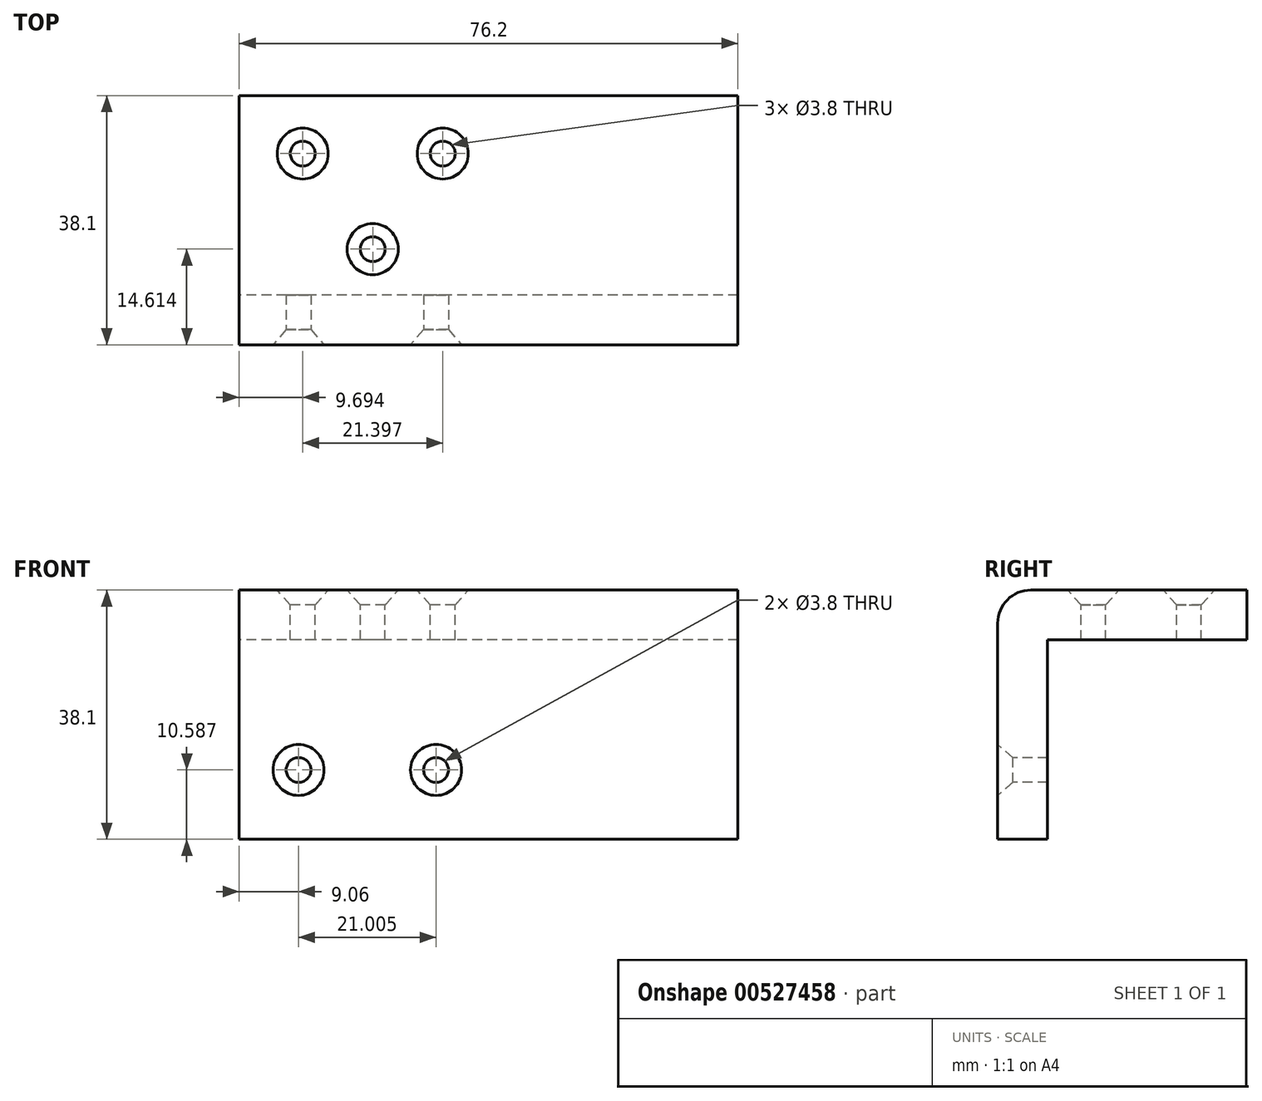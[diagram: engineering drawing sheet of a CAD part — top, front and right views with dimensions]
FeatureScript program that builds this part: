
annotation { "Feature Type Name" : "Feature", "Feature Type Description" : "" }
export const myFeature = defineFeature(function(context is Context, id is Id, definition is map)
    precondition{}
    {
        {
            var Q0;
            Q0=qCreatedBy(makeId("Right.planeOp"),FACE);
            var sketch = newSketch(context, id + "F0", { "sketchPlane" : qUnion([Q0])});
            skLineSegment(sketch, "E0.bottom", {"start": v(-7.62, 7.62) * mm, "end": v(30.48, 7.62) * mm});
            skLineSegment(sketch, "E0.top", {"start": v(-7.62, -30.48) * mm, "end": v(0, -30.48) * mm});
            skLineSegment(sketch, "E0.left", {"start": v(-7.62, 7.62) * mm, "end": v(-7.62, -30.48) * mm});
            skLineSegment(sketch, "E0.right", {"start": v(30.48, 7.62) * mm, "end": v(30.48, 0) * mm});
            skLineSegment(sketch, "E1", {"start": v(0, -30.48) * mm, "end": v(0, 0) * mm});
            skLineSegment(sketch, "E2", {"start": v(0, 0) * mm, "end": v(30.48, 0) * mm});
            skSolve(sketch);
        }
        {
            var Q0;
            Q0=makeQuery(id+"F0.imprint","IMPRINT",FACE,{"disambiguationData":[TD([[makeQuery(id+"F0.imprint","IMPRINT",EDGE,{"derivedFrom":sQuery(id+"F0.wireOp",EDGE,"E0.bottom")}),-1.0]])]});
            extrude(context, id + "F1", {"entities" : qUnion([Q0]), "endBound" : BoundingType.SYMMETRIC, "depth" : 76.2 * mm, "offsetDistance" : 25.4 * mm});
        }
        {
            var Q0;
            Q0=makeQuery(id+"F1.opExtrude","SWEPT_FACE",FACE,{"disambiguationData":[OSD([sQuery(id+"F0.wireOp",EDGE,"E0.bottom")])]});
            var sketch = newSketch(context, id + "F2", { "sketchPlane" : qUnion([Q0])});
            skLineSegment(sketch, "E3.bottom", {"start": v(-7, -7.62) * mm, "end": v(-28.4, -7.62) * mm});
            skLineSegment(sketch, "E3.top", {"start": v(-7, 21.6) * mm, "end": v(-28.4, 21.6) * mm});
            skLineSegment(sketch, "E3.left", {"start": v(-7, -7.62) * mm, "end": v(-7, 21.6) * mm});
            skLineSegment(sketch, "E3.right", {"start": v(-28.4, -7.62) * mm, "end": v(-28.4, 21.6) * mm});
            skPoint(sketch, "E4", {"position": v(-28.4, 21.6) * mm});
            skPoint(sketch, "E5", {"position": v(-7, 21.6) * mm});
            skLineSegment(sketch, "E6", {"start": v(-17.7, 21.6) * mm, "end": v(-17.7, -7.62) * mm});
            skPoint(sketch, "E7", {"position": v(-17.7, 7) * mm});
            skSolve(sketch);
        }
        {
            var Q0;
            Q0=sQuery(id+"F2.wireOp",VERTEX,"E4");
            var Q1;
            Q1=sQuery(id+"F2.wireOp",VERTEX,"E5");
            var Q2;
            Q2=sQuery(id+"F2.wireOp",VERTEX,"E7");
            var Q3;
            Q3=makeQuery(id+"F1.opExtrude","SWEPT_BODY",BODY,{"disambiguationData":[OSD([sQuery(id+"F0.wireOp",EDGE,"E0.bottom"),sQuery(id+"F0.wireOp",EDGE,"E0.top"),sQuery(id+"F0.wireOp",EDGE,"E0.left"),sQuery(id+"F0.wireOp",EDGE,"E0.right"),sQuery(id+"F0.wireOp",EDGE,"E1"),sQuery(id+"F0.wireOp",EDGE,"E2")])]});
            hole(context, id + "F3", {"style" : HoleStyle.C_SINK, "endStyle" : HoleEndStyle.THROUGH, "standardTappedOrClearance" : lookupTablePath({ "standard" : "ANSI", "fit" : "Normal (ASME)", "size" : "#6", "type" : "Clearance" }), "standardBlindInLast" : lookupTablePath({ "fit" : "Free", "standard" : "ANSI", "size" : "#6", "type" : "Clearance" }), "holeDiameter" : 3.8 * mm, "cSinkDiameter" : 7.8 * mm, "cSinkAngle" : 82 * degree, "majorDiameter" : 6.35 * mm, "isTappedThrough" : true, "tappedDepth" : 12.7 * mm, "tapClearance" : 3, "locations" : qUnion([Q0, Q1, Q2]), "scope" : qUnion([Q3])});
        }
        {
            var Q0;
            Q0=makeQuery(id+"F1.opExtrude","SWEPT_EDGE",EDGE,{"disambiguationData":[OSD([sQuery(id+"F0.wireOp",EDGE,"E0.bottom"),sQuery(id+"F0.wireOp",EDGE,"E0.left")])]});
            fillet(context, id + "F4", {"entities" : qUnion([Q0]), "radius" : 5.08 * mm, "tangentPropagation" : true, "allowEdgeOverflow" : false});
        }
        {
            var Q0;
            Q0=makeQuery(id+"F1.opExtrude","SWEPT_FACE",FACE,{"disambiguationData":[OSD([sQuery(id+"F0.wireOp",EDGE,"E0.left")])]});
            var sketch = newSketch(context, id + "F5", { "sketchPlane" : qUnion([Q0])});
            skLineSegment(sketch, "E8.bottom", {"start": v(-8.03, -30.48) * mm, "end": v(-29.04, -30.48) * mm});
            skLineSegment(sketch, "E8.top", {"start": v(-8.03, -19.9) * mm, "end": v(-29.04, -19.9) * mm});
            skLineSegment(sketch, "E8.left", {"start": v(-8.03, -30.48) * mm, "end": v(-8.03, -19.9) * mm});
            skLineSegment(sketch, "E8.right", {"start": v(-29.04, -30.48) * mm, "end": v(-29.04, -19.9) * mm});
            skPoint(sketch, "E9", {"position": v(-8.03, -19.9) * mm});
            skPoint(sketch, "E10", {"position": v(-29.04, -19.9) * mm});
            skSolve(sketch);
        }
        {
            var Q0;
            Q0=sQuery(id+"F5.wireOp",VERTEX,"E9");
            var Q1;
            Q1=sQuery(id+"F5.wireOp",VERTEX,"E10");
            var Q2;
            Q2=makeQuery(id+"F1.opExtrude","SWEPT_BODY",BODY,{"disambiguationData":[OSD([sQuery(id+"F0.wireOp",EDGE,"E0.bottom"),sQuery(id+"F0.wireOp",EDGE,"E0.top"),sQuery(id+"F0.wireOp",EDGE,"E0.left"),sQuery(id+"F0.wireOp",EDGE,"E0.right"),sQuery(id+"F0.wireOp",EDGE,"E1"),sQuery(id+"F0.wireOp",EDGE,"E2")])]});
            hole(context, id + "F6", {"style" : HoleStyle.C_SINK, "endStyle" : HoleEndStyle.THROUGH, "standardTappedOrClearance" : lookupTablePath({ "standard" : "ANSI", "fit" : "Normal (ASME)", "size" : "#6", "type" : "Clearance" }), "standardBlindInLast" : lookupTablePath({ "fit" : "Free", "standard" : "ANSI", "size" : "#6", "type" : "Clearance" }), "holeDiameter" : 3.8 * mm, "cSinkDiameter" : 7.8 * mm, "cSinkAngle" : 82 * degree, "majorDiameter" : 6.35 * mm, "isTappedThrough" : true, "tappedDepth" : 12.7 * mm, "tapClearance" : 3, "locations" : qUnion([Q0, Q1]), "scope" : qUnion([Q2])});
        }
    });
